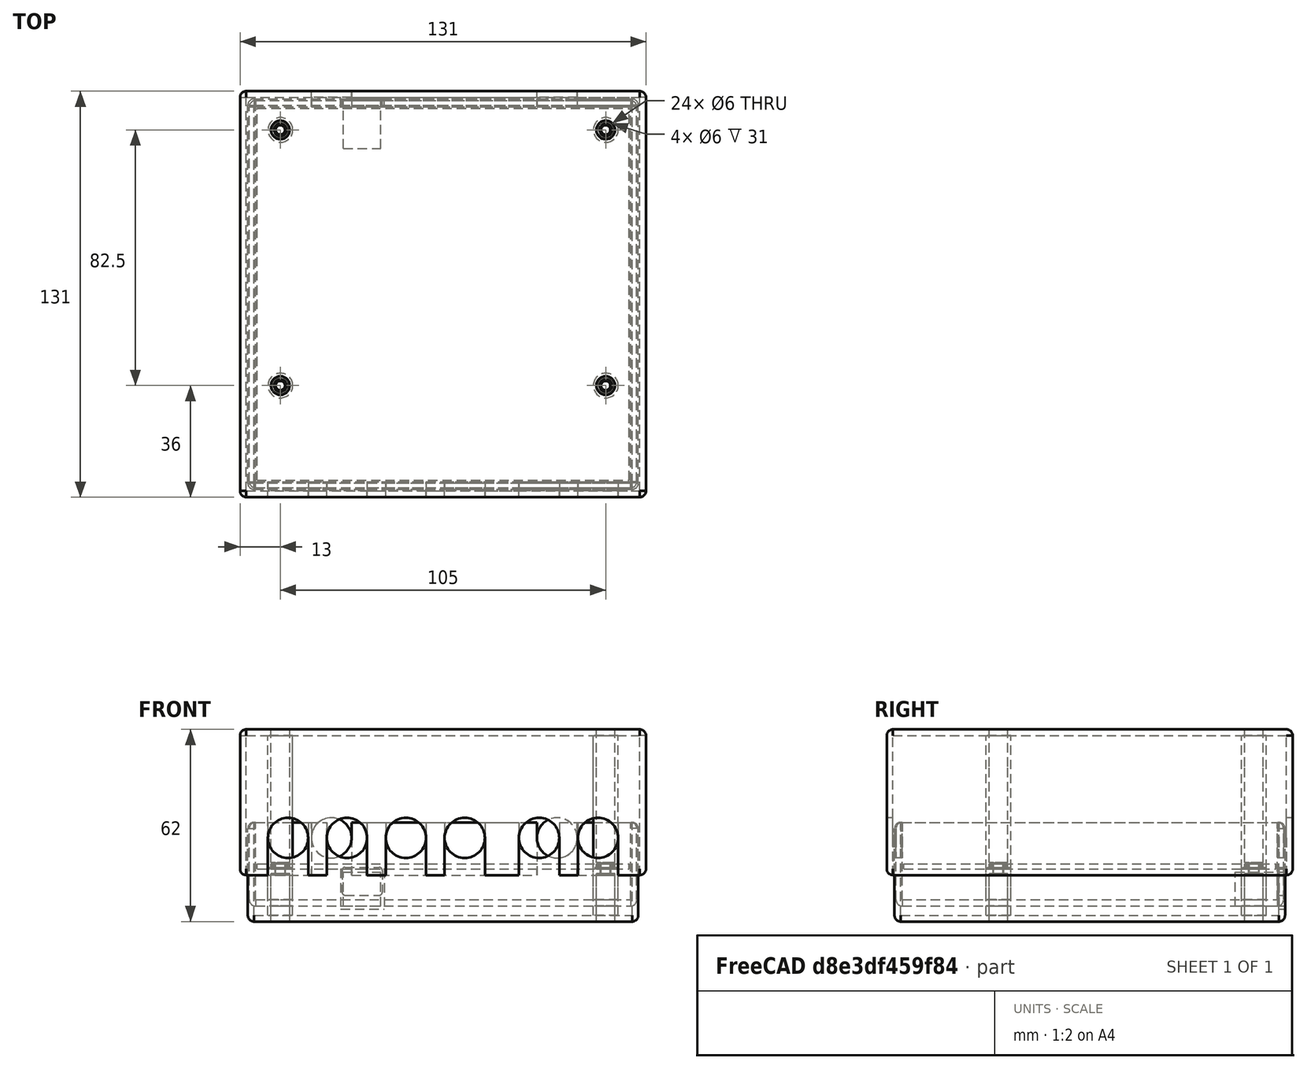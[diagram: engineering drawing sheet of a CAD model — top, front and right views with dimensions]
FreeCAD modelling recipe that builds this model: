
FCSTD DOCUMENT  (FreeCAD 0.14R3700 (Git))
Label: board
License: CC-BY 3.0
LicenseURL: http://creativecommons.org/licenses/by/3.0/
objects: Part::FeaturePython×65, Part::Cylinder×24, Part::MultiFuse×21, Part::Cut×21, Part::Box×17, Part::Offset×4, App::DocumentObjectGroup×3, Part::Feature×1, Part::Fillet×1
note: 154 computed .brp shape members not serialized (recipe doc carries the construction recipe); baked Part::Feature solids carry a one-line shape summary decoded from their .brp

FEATURE [Part::Box] Box  label="Cube"
  Height = 1.6
  Length = 120
  Width = 120
FEATURE [Part::Cylinder] Cylinder
  Angle = 360
  Height = 10
  Placement = pos=(7.5,30.5,-5) rot=(0,0,1;0rad)
  Radius = 3
FEATURE [Part::FeaturePython] Clone  label="Clone of Cylinder"  # Draft clone (typed FeaturePython)
  Objects = -> [Cylinder]
  Placement = pos=(7.5,113,-5) rot=(0,0,1;0rad)
  Scale = (1,1,1)
FEATURE [Part::FeaturePython] Clone001  label="Clone of Cylinder001"  # Draft clone (typed FeaturePython)
  Objects = -> [Cylinder]
  Placement = pos=(112.5,30.5,-5) rot=(0,0,1;0rad)
  Scale = (1,1,1)
FEATURE [Part::FeaturePython] Clone002  label="Clone of Cylinder002"  # Draft clone (typed FeaturePython)
  Objects = -> [Cylinder]
  Placement = pos=(112.5,113,-5) rot=(0,0,1;0rad)
  Scale = (1,1,1)
FEATURE [Part::MultiFuse] Fusion
  Shapes = -> [Cylinder,Clone001,Clone,Clone002]
FEATURE [Part::Cut] Cut  label="board"
  Base = -> Box
  Tool = -> Fusion
FEATURE [Part::Feature] _31_5431_10rfx  label="bnc"
  Placement = pos=(9.975,15.5,2.1) rot=(0.57735,-0.57735,-0.57735;2.0944rad)
  shape: bbox 14.98 x 40.02 x 19.89 mm, 151 faces, 0 solids (baked)
FEATURE [Part::FeaturePython] Clone003  label="bnc02"  # Draft clone (typed FeaturePython)
  Objects = -> [_31_5431_10rfx]
  Placement = pos=(28.975,15.5,2.1) rot=(0.57735,-0.57735,-0.57735;2.0944rad)
  Scale = (1,1,1)
FEATURE [Part::FeaturePython] Clone004  label="bnc03"  # Draft clone (typed FeaturePython)
  Objects = -> [_31_5431_10rfx]
  Placement = pos=(47.975,15.5,2.1) rot=(0.57735,-0.57735,-0.57735;2.0944rad)
  Scale = (1,1,1)
FEATURE [Part::FeaturePython] Clone005  label="bnc04"  # Draft clone (typed FeaturePython)
  Objects = -> [_31_5431_10rfx]
  Placement = pos=(66.975,15.5,2.1) rot=(0.57735,-0.57735,-0.57735;2.0944rad)
  Scale = (1,1,1)
FEATURE [Part::FeaturePython] Clone006  label="bnc05"  # Draft clone (typed FeaturePython)
  Objects = -> [_31_5431_10rfx]
  Placement = pos=(90.975,15.5,2.1) rot=(0.57735,-0.57735,-0.57735;2.0944rad)
  Scale = (1,1,1)
FEATURE [Part::FeaturePython] Clone007  label="bnc06"  # Draft clone (typed FeaturePython)
  Objects = -> [_31_5431_10rfx]
  Placement = pos=(109.975,15.5,2.1) rot=(0.57735,-0.57735,-0.57735;2.0944rad)
  Scale = (1,1,1)
FEATURE [Part::FeaturePython] Clone008  label="bnc07"  # Draft clone (typed FeaturePython)
  Objects = -> [_31_5431_10rfx]
  Placement = pos=(96.775,104.5,2.1) rot=(0.57735,0.57735,0.57735;2.0944rad)
  Scale = (1,1,1)
FEATURE [Part::Box] Box001  label="usb"
  Height = 11
  Length = 12.04
  Placement = pos=(27.851,107,-12) rot=(0,0,1;0rad)
  Width = 16
FEATURE [Part::FeaturePython] Clone009  label="bnc08"  # Draft clone (typed FeaturePython)
  Objects = -> [_31_5431_10rfx]
  Placement = pos=(24.025,104.5,2.1) rot=(0.57735,0.57735,0.57735;2.0944rad)
  Scale = (1,1,1)
FEATURE [Part::Cylinder] Cylinder001
  Angle = 360
  Height = 1.6
  Placement = pos=(7.5,30.5,0) rot=(0,0,1;0rad)
  Radius = 2.5
FEATURE [Part::Cylinder] Cylinder002
  Angle = 360
  Height = 10
  Placement = pos=(7.5,30.5,-9.6) rot=(0,0,1;0rad)
  Radius = 4
FEATURE [Part::MultiFuse] Fusion001
  Shapes = -> [Cylinder001,Cylinder002]
FEATURE [Part::Cylinder] Cylinder003
  Angle = 360
  Height = 9
  Placement = pos=(7.5,30.5,-10.6) rot=(0,0,1;0rad)
  Radius = 3
FEATURE [Part::Cut] Cut001
  Base = -> Fusion001
  Tool = -> Cylinder003
FEATURE [Part::Cylinder] Cylinder004
  Angle = 360
  Height = 9
  Placement = pos=(7.5,30.5,-5.6) rot=(0,0,1;0rad)
  Radius = 1.5
FEATURE [Part::Cut] Cut002
  Base = -> Cut001
  Tool = -> Cylinder004
FEATURE [Part::FeaturePython] Clone010  label="Clone of Cut002"  # Draft clone (typed FeaturePython)
  Objects = -> [Cut002]
  Placement = pos=(105,0,0) rot=(0,0,1;0rad)
  Scale = (1,1,1)
FEATURE [Part::FeaturePython] Clone011  label="Clone of Cut003"  # Draft clone (typed FeaturePython)
  Objects = -> [Cut002]
  Placement = pos=(0,82.5,0) rot=(0,0,1;0rad)
  Scale = (1,1,1)
FEATURE [Part::FeaturePython] Clone012  label="Clone of Cut004"  # Draft clone (typed FeaturePython)
  Objects = -> [Cut002]
  Placement = pos=(105,82.5,0) rot=(0,0,1;0rad)
  Scale = (1,1,1)
FEATURE [Part::Box] Box002  label="Cube001"
  Height = 23
  Length = 121
  Placement = pos=(-0.5,-0.5,-10) rot=(0,0,1;0rad)
  Width = 121
FEATURE [Part::Offset] Offset
  Fill = false
  Intersection = false
  Join = 0
  Mode = 0
  SelfIntersection = false
  Source = -> Box002
  Value = 2
FEATURE [Part::Cylinder] Cylinder005
  Angle = 360
  Height = 10
  Placement = pos=(10,3,10) rot=(1,0,0;1.5708rad)
  Radius = 6.5
FEATURE [Part::Box] Box003  label="Cube002"
  Height = 10
  Length = 13
  Placement = pos=(3.5,-7,10) rot=(0,0,1;0rad)
  Width = 10
FEATURE [Part::MultiFuse] Fusion002  label="bnc-cut"
  Shapes = -> [Cylinder005,Box003]
FEATURE [Part::FeaturePython] Clone013  label="Clone of bnc-cut"  # Draft clone (typed FeaturePython)
  Objects = -> [Fusion002]
  Placement = pos=(19,0,0) rot=(0,0,1;0rad)
  Scale = (1,1,1)
FEATURE [Part::FeaturePython] Clone014  label="Clone of bnc-cut001"  # Draft clone (typed FeaturePython)
  Objects = -> [Fusion002]
  Placement = pos=(38,0,0) rot=(0,0,1;0rad)
  Scale = (1,1,1)
FEATURE [Part::FeaturePython] Clone015  label="Clone of bnc-cut002"  # Draft clone (typed FeaturePython)
  Objects = -> [Fusion002]
  Placement = pos=(57,0,0) rot=(0,0,1;0rad)
  Scale = (1,1,1)
FEATURE [Part::FeaturePython] Clone016  label="Clone of bnc-cut003"  # Draft clone (typed FeaturePython)
  Objects = -> [Fusion002]
  Placement = pos=(81,0,0) rot=(0,0,1;0rad)
  Scale = (1,1,1)
FEATURE [Part::FeaturePython] Clone017  label="Clone of bnc-cut004"  # Draft clone (typed FeaturePython)
  Objects = -> [Fusion002]
  Placement = pos=(100,0,0) rot=(0,0,1;0rad)
  Scale = (1,1,1)
FEATURE [Part::FeaturePython] Clone018  label="Clone of bnc-cut005"  # Draft clone (typed FeaturePython)
  Objects = -> [Fusion002]
  Placement = pos=(14,122,0) rot=(0,0,1;0rad)
  Scale = (1,1,1)
FEATURE [Part::FeaturePython] Clone019  label="Clone of bnc-cut006"  # Draft clone (typed FeaturePython)
  Objects = -> [Fusion002]
  Placement = pos=(86.8,122,0) rot=(0,0,1;0rad)
  Scale = (1,1,1)
FEATURE [Part::Box] Box004  label="Cube003"
  Height = 30
  Length = 121
  Placement = pos=(-0.5,-0.5,-10) rot=(0,0,1;0rad)
  Width = 121
FEATURE [Part::MultiFuse] Fusion003
  Shapes = -> [Clone013,Box004,Clone015,Clone017,Clone018,Clone014,Clone019,Clone016,Fusion002]
FEATURE [Part::Cut] Cut003
  Base = -> Offset
  Tool = -> Fusion003
FEATURE [Part::Box] Box005  label="Cube004"
  Height = 9
  Length = 13
  Placement = pos=(27.4,115,0) rot=(0,0,1;0rad)
  Width = 10
FEATURE [Part::Fillet] Fillet
  Base = -> Box005
  Edges = 12 edges r=1: [Edge1,Edge2,Edge3,Edge4,Edge5,Edge6,Edge7,Edge8,Edge9,Edge10,Edge11,Edge12]
  Placement = pos=(0,0,-8.5) rot=(0,0,1;0rad)
FEATURE [Part::Cut] Cut004
  Base = -> Cut003
  Tool = -> Fillet
FEATURE [Part::Cylinder] Cylinder006
  Angle = 360
  Height = 10
  Placement = pos=(7.5,30.5,-15.6) rot=(0,0,1;0rad)
  Radius = 4
FEATURE [Part::FeaturePython] Clone020  label="Clone of Cylinder006"  # Draft clone (typed FeaturePython)
  Objects = -> [Cylinder006]
  Placement = pos=(7.5,113,-15.6) rot=(0,0,1;0rad)
  Scale = (1,1,1)
FEATURE [Part::FeaturePython] Clone021  label="Clone of Cylinder007"  # Draft clone (typed FeaturePython)
  Objects = -> [Cylinder006]
  Placement = pos=(112.5,30.5,-15.6) rot=(0,0,1;0rad)
  Scale = (1,1,1)
FEATURE [Part::FeaturePython] Clone022  label="Clone of Cylinder008"  # Draft clone (typed FeaturePython)
  Objects = -> [Cylinder006]
  Placement = pos=(112.5,113,-15.6) rot=(0,0,1;0rad)
  Scale = (1,1,1)
FEATURE [Part::MultiFuse] Fusion004
  Shapes = -> [Cylinder006,Clone020,Clone021,Clone022]
FEATURE [Part::Cut] Cut005
  Base = -> Cut004
  Tool = -> Fusion004
FEATURE [Part::MultiFuse] Fusion005
  Shapes = -> [Cut002,Clone010,Clone011,Clone012,Cut005]
FEATURE [Part::Box] Box006  label="Cube005"
  Height = 40
  Length = 126
  Placement = pos=(-3,-3,3) rot=(0,0,1;0rad)
  Width = 126
FEATURE [Part::Box] Box007  label="Cube006"
  Height = 40
  Length = 34
  Placement = pos=(35,115,2) rot=(0,0,1;0rad)
  Width = 2
FEATURE [App::DocumentObjectGroup] Group  label="pcb"
  Group = -> [Cut,_31_5431_10rfx,Clone003,Clone004,Clone005,Clone006,Clone007,Clone008,Box001,Clone009,Box007]
FEATURE [Part::Offset] Offset001
  Fill = false
  Intersection = false
  Join = 0
  Mode = 0
  SelfIntersection = false
  Source = -> Box006
  Value = 2
FEATURE [Part::Box] Box008  label="Cube007"
  Height = 45
  Length = 126
  Placement = pos=(-3,-3,-2) rot=(0,0,1;0rad)
  Width = 126
FEATURE [Part::Cut] Cut006
  Base = -> Offset001
  Tool = -> Box008
FEATURE [Part::Cylinder] Cylinder007
  Angle = 360
  Height = 42
  Placement = pos=(7.5,30.5,1.6) rot=(0,0,1;0rad)
  Radius = 4
FEATURE [Part::Cylinder] Cylinder008
  Angle = 360
  Height = 9
  Placement = pos=(7.5,30.5,-0.6) rot=(0,0,1;0rad)
  Radius = 1.5
FEATURE [Part::Cylinder] Cylinder009
  Angle = 360
  Height = 43
  Placement = pos=(7.5,30.5,3.4) rot=(0,0,1;0rad)
  Radius = 3
FEATURE [Part::Cut] Cut007
  Base = -> Cylinder007
  Tool = -> Cylinder008
FEATURE [Part::FeaturePython] Clone023  label="Clone of Cut007"  # Draft clone (typed FeaturePython)
  Objects = -> [Cut007]
  Placement = pos=(105,0,0) rot=(0,0,1;0rad)
  Scale = (1,1,1)
FEATURE [Part::FeaturePython] Clone024  label="Clone of Cut008"  # Draft clone (typed FeaturePython)
  Objects = -> [Cut007]
  Placement = pos=(105,82.5,0) rot=(0,0,1;0rad)
  Scale = (1,1,1)
FEATURE [Part::FeaturePython] Clone025  label="Clone of Cut009"  # Draft clone (typed FeaturePython)
  Objects = -> [Cut007]
  Placement = pos=(0,82.5,0) rot=(0,0,1;0rad)
  Scale = (1,1,1)
FEATURE [Part::MultiFuse] Fusion006
  Shapes = -> [Cut006,Clone023,Cut007,Clone024,Clone025]
FEATURE [Part::FeaturePython] Clone026  label="Clone of Cylinder009"  # Draft clone (typed FeaturePython)
  Objects = -> [Cylinder009]
  Placement = pos=(112.5,30.5,3.4) rot=(0,0,1;0rad)
  Scale = (1,1,1)
FEATURE [Part::FeaturePython] Clone027  label="Clone of Cylinder010"  # Draft clone (typed FeaturePython)
  Objects = -> [Cylinder009]
  Placement = pos=(112.5,113,3.4) rot=(0,0,1;0rad)
  Scale = (1,1,1)
FEATURE [Part::FeaturePython] Clone028  label="Clone of Cylinder011"  # Draft clone (typed FeaturePython)
  Objects = -> [Cylinder009]
  Placement = pos=(7.5,113,3.4) rot=(0,0,1;0rad)
  Scale = (1,1,1)
FEATURE [Part::MultiFuse] Fusion007
  Shapes = -> [Cylinder009,Clone026,Clone027,Clone028]
FEATURE [Part::Cut] Cut008
  Base = -> Fusion006
  Tool = -> Fusion007
FEATURE [Part::Cylinder] Cylinder010
  Angle = 360
  Height = 3
  Placement = pos=(7.5,30.5,-12) rot=(0,0,1;0rad)
  Radius = 4
FEATURE [Part::Cylinder] Cylinder011
  Angle = 360
  Height = 8.6
  Placement = pos=(7.5,30.5,-15) rot=(0,0,1;0rad)
  Radius = 3
FEATURE [Part::Cut] Cut009
  Base = -> Cylinder010
  Tool = -> Cylinder011
FEATURE [Part::FeaturePython] Clone029  label="Clone of Cut010"  # Draft clone (typed FeaturePython)
  Objects = -> [Cut009]
  Placement = pos=(0,82.5,0) rot=(0,0,1;0rad)
  Scale = (1,1,1)
FEATURE [Part::FeaturePython] Clone030  label="Clone of Cut011"  # Draft clone (typed FeaturePython)
  Objects = -> [Cut009]
  Placement = pos=(105,0,0) rot=(0,0,1;0rad)
  Scale = (1,1,1)
FEATURE [Part::FeaturePython] Clone031  label="Clone of Cut012"  # Draft clone (typed FeaturePython)
  Objects = -> [Cut009]
  Placement = pos=(105,82.5,0) rot=(0,0,1;0rad)
  Scale = (1,1,1)
FEATURE [Part::MultiFuse] Fusion008
  Shapes = -> [Cut009,Clone029,Clone031,Clone030,Fusion005]
FEATURE [App::DocumentObjectGroup] Group001  label="bottom"
  Group = -> [Fusion005,Cut009,Clone029,Clone031,Clone030,Fusion008]
FEATURE [Part::Cylinder] Cylinder012
  Angle = 360
  Height = 10
  Placement = pos=(10,3,10) rot=(1,0,0;1.5708rad)
  Radius = 6.5
FEATURE [Part::Box] Box009  label="Cube008"
  Height = 10
  Length = 13
  Placement = pos=(3.5,-7,0) rot=(0,0,1;0rad)
  Width = 10
FEATURE [Part::MultiFuse] Fusion009  label="bnc-cut-top"
  Shapes = -> [Cylinder012,Box009]
FEATURE [Part::FeaturePython] Clone032  label="Clone of bnc-cut-top"  # Draft clone (typed FeaturePython)
  Objects = -> [Fusion009]
  Placement = pos=(19,0,0) rot=(0,0,1;0rad)
  Scale = (1,1,1)
FEATURE [Part::FeaturePython] Clone033  label="Clone of bnc-cut-top001"  # Draft clone (typed FeaturePython)
  Objects = -> [Fusion009]
  Placement = pos=(38,0,0) rot=(0,0,1;0rad)
  Scale = (1,1,1)
FEATURE [Part::FeaturePython] Clone034  label="Clone of bnc-cut-top002"  # Draft clone (typed FeaturePython)
  Objects = -> [Fusion009]
  Placement = pos=(57,0,0) rot=(0,0,1;0rad)
  Scale = (1,1,1)
FEATURE [Part::FeaturePython] Clone035  label="Clone of bnc-cut-top003"  # Draft clone (typed FeaturePython)
  Objects = -> [Fusion009]
  Placement = pos=(81,0,0) rot=(0,0,1;0rad)
  Scale = (1,1,1)
FEATURE [Part::FeaturePython] Clone036  label="Clone of bnc-cut-top004"  # Draft clone (typed FeaturePython)
  Objects = -> [Fusion009]
  Placement = pos=(100,0,0) rot=(0,0,1;0rad)
  Scale = (1,1,1)
FEATURE [Part::FeaturePython] Clone037  label="Clone of bnc-cut-top005"  # Draft clone (typed FeaturePython)
  Objects = -> [Fusion009]
  Placement = pos=(14,125,0) rot=(0,0,1;0rad)
  Scale = (1,1,1)
FEATURE [Part::FeaturePython] Clone038  label="Clone of bnc-cut-top006"  # Draft clone (typed FeaturePython)
  Objects = -> [Fusion009]
  Placement = pos=(86.8,125,0) rot=(0,0,1;0rad)
  Scale = (1,1,1)
FEATURE [Part::MultiFuse] Fusion010
  Shapes = -> [Fusion009,Clone033,Clone032,Clone034,Clone035,Clone036,Clone037,Clone038]
FEATURE [Part::Cut] Cut010
  Base = -> Cut008
  Tool = -> Fusion010
FEATURE [App::DocumentObjectGroup] Group002  label="top"
  Group = -> [Cut010]
FEATURE [Part::Box] Box010  label="Cube009"
  Height = 28
  Length = 122
  Placement = pos=(-1,-1,-15) rot=(0,0,1;0rad)
  Width = 122
FEATURE [Part::Offset] Offset002
  Fill = false
  Intersection = false
  Join = 0
  Mode = 0
  SelfIntersection = false
  Source = -> Box010
  Value = 2
FEATURE [Part::Box] Box011  label="Cube010"
  Height = 37
  Length = 122
  Placement = pos=(-1,-1,-15) rot=(0,0,1;0rad)
  Width = 122
FEATURE [Part::Cut] Cut011
  Base = -> Offset002
  Tool = -> Box011
FEATURE [Part::Box] Box012  label="Cube011"
  Height = 13
  Length = 14
  Placement = pos=(27,116,-13) rot=(0,0,1;0rad)
  Width = 10
FEATURE [Part::Cut] Cut012
  Base = -> Cut011
  Tool = -> Box012
FEATURE [Part::Cylinder] Cylinder013
  Angle = 360
  Height = 10
  Placement = pos=(10,2,10) rot=(1,0,0;1.5708rad)
  Radius = 6.5
FEATURE [Part::Box] Box013  label="Cube012"
  Height = 10
  Length = 13
  Placement = pos=(3.5,-8,10) rot=(0,0,1;0rad)
  Width = 10
FEATURE [Part::MultiFuse] Fusion011  label="bnc-cut001"
  Shapes = -> [Cylinder013,Box013]
FEATURE [Part::FeaturePython] Clone039  label="Clone of bnc-cut007"  # Draft clone (typed FeaturePython)
  Objects = -> [Fusion011]
  Placement = pos=(19,0,0) rot=(0,0,1;0rad)
  Scale = (1,1,1)
FEATURE [Part::FeaturePython] Clone040  label="Clone of bnc-cut008"  # Draft clone (typed FeaturePython)
  Objects = -> [Fusion011]
  Placement = pos=(38,0,0) rot=(0,0,1;0rad)
  Scale = (1,1,1)
FEATURE [Part::FeaturePython] Clone041  label="Clone of bnc-cut009"  # Draft clone (typed FeaturePython)
  Objects = -> [Fusion011]
  Placement = pos=(57,0,0) rot=(0,0,1;0rad)
  Scale = (1,1,1)
FEATURE [Part::FeaturePython] Clone042  label="Clone of bnc-cut010"  # Draft clone (typed FeaturePython)
  Objects = -> [Fusion011]
  Placement = pos=(81,0,0) rot=(0,0,1;0rad)
  Scale = (1,1,1)
FEATURE [Part::FeaturePython] Clone043  label="Clone of bnc-cut011"  # Draft clone (typed FeaturePython)
  Objects = -> [Fusion011]
  Placement = pos=(100,0,0) rot=(0,0,1;0rad)
  Scale = (1,1,1)
FEATURE [Part::FeaturePython] Clone044  label="Clone of bnc-cut012"  # Draft clone (typed FeaturePython)
  Objects = -> [Fusion011]
  Placement = pos=(14,124,0) rot=(0,0,1;0rad)
  Scale = (1,1,1)
FEATURE [Part::FeaturePython] Clone045  label="Clone of bnc-cut013"  # Draft clone (typed FeaturePython)
  Objects = -> [Fusion011]
  Placement = pos=(86.8,124,0) rot=(0,0,1;0rad)
  Scale = (1,1,1)
FEATURE [Part::MultiFuse] Fusion012  label="bnc-full-cut"
  Shapes = -> [Fusion011,Clone042,Clone043,Clone044,Clone041,Clone045,Clone040,Clone039]
FEATURE [Part::Cut] Cut013
  Base = -> Cut012
  Tool = -> Fusion012
FEATURE [Part::Cylinder] Cylinder014
  Angle = 360
  Height = 10
  Placement = pos=(7.5,30.5,-4) rot=(0,0,1;0rad)
  Radius = 1.7
FEATURE [Part::Cylinder] Cylinder015
  Angle = 360
  Height = 11.6
  Placement = pos=(7.5,30.5,-10) rot=(0,0,1;0rad)
  Radius = 2.5
FEATURE [Part::Cylinder] Cylinder016
  Angle = 360
  Height = 15
  Placement = pos=(7.5,30.5,-15) rot=(0,0,1;0rad)
  Radius = 4
FEATURE [Part::MultiFuse] Fusion013
  Shapes = -> [Cylinder015,Cylinder016]
FEATURE [Part::Cylinder] Cylinder017
  Angle = 360
  Height = 15
  Placement = pos=(7.5,30.5,-17) rot=(0,0,1;0rad)
  Radius = 3
FEATURE [Part::MultiFuse] Fusion014
  Shapes = -> [Cylinder017,Cylinder014]
FEATURE [Part::Cut] Cut014  label="stand-bottom"
  Base = -> Fusion013
  Tool = -> Fusion014
FEATURE [Part::FeaturePython] Clone046  label="Clone of stand-bottom"  # Draft clone (typed FeaturePython)
  Objects = -> [Cut014]
  Placement = pos=(105,0,0) rot=(0,0,1;0rad)
  Scale = (1,1,1)
FEATURE [Part::FeaturePython] Clone047  label="Clone of stand-bottom001"  # Draft clone (typed FeaturePython)
  Objects = -> [Cut014]
  Placement = pos=(105,82.5,0) rot=(0,0,1;0rad)
  Scale = (1,1,1)
FEATURE [Part::FeaturePython] Clone048  label="Clone of stand-bottom002"  # Draft clone (typed FeaturePython)
  Objects = -> [Cut014]
  Placement = pos=(0,82.5,0) rot=(0,0,1;0rad)
  Scale = (1,1,1)
FEATURE [Part::MultiFuse] Fusion015
  Shapes = -> [Cut013,Cut014,Clone046,Clone047,Clone048]
FEATURE [Part::Cylinder] Cylinder018
  Angle = 360
  Height = 15
  Placement = pos=(7.5,30.5,-20) rot=(0,0,1;0rad)
  Radius = 3
FEATURE [Part::FeaturePython] Clone049  label="Clone of Cylinder018"  # Draft clone (typed FeaturePython)
  Objects = -> [Cylinder018]
  Placement = pos=(112.5,30.5,-20) rot=(0,0,1;0rad)
  Scale = (1,1,1)
FEATURE [Part::FeaturePython] Clone050  label="Clone of Cylinder019"  # Draft clone (typed FeaturePython)
  Objects = -> [Cylinder018]
  Placement = pos=(112.5,113,-20) rot=(0,0,1;0rad)
  Scale = (1,1,1)
FEATURE [Part::FeaturePython] Clone051  label="Clone of Cylinder020"  # Draft clone (typed FeaturePython)
  Objects = -> [Cylinder018]
  Placement = pos=(7.5,113,-20) rot=(0,0,1;0rad)
  Scale = (1,1,1)
FEATURE [Part::MultiFuse] Fusion016
  Shapes = -> [Cylinder018,Clone049,Clone050,Clone051]
FEATURE [Part::Cut] Cut015  label="bottom-v02"
  Base = -> Fusion015
  Tool = -> Fusion016
FEATURE [Part::Box] Box014  label="Cube013"
  Height = 43
  Length = 127
  Placement = pos=(-3.5,-3.5,0) rot=(0,0,1;0rad)
  Width = 127
FEATURE [Part::Offset] Offset003
  Fill = false
  Intersection = false
  Join = 0
  Mode = 0
  SelfIntersection = false
  Source = -> Box014
  Value = 2
FEATURE [Part::Box] Box015  label="Cube014"
  Height = 46
  Length = 127
  Placement = pos=(-3.5,-3.5,-3) rot=(0,0,1;0rad)
  Width = 127
FEATURE [Part::Cut] Cut016
  Base = -> Offset003
  Tool = -> Box015
FEATURE [Part::Cylinder] Cylinder019
  Angle = 360
  Height = 10
  Placement = pos=(10,0,10) rot=(1,0,0;1.5708rad)
  Radius = 6.5
FEATURE [Part::Box] Box016  label="Cube015"
  Height = 14
  Length = 13
  Placement = pos=(3.5,-10,-4) rot=(0,0,1;0rad)
  Width = 10
FEATURE [Part::MultiFuse] Fusion017  label="bnc-cut-top001"
  Shapes = -> [Cylinder019,Box016]
FEATURE [Part::FeaturePython] Clone052  label="Clone of bnc-cut-top007"  # Draft clone (typed FeaturePython)
  Objects = -> [Fusion017]
  Placement = pos=(19,0,0) rot=(0,0,1;0rad)
  Scale = (1,1,1)
FEATURE [Part::FeaturePython] Clone053  label="Clone of bnc-cut-top008"  # Draft clone (typed FeaturePython)
  Objects = -> [Fusion017]
  Placement = pos=(38,0,0) rot=(0,0,1;0rad)
  Scale = (1,1,1)
FEATURE [Part::FeaturePython] Clone054  label="Clone of bnc-cut-top009"  # Draft clone (typed FeaturePython)
  Objects = -> [Fusion017]
  Placement = pos=(57,0,0) rot=(0,0,1;0rad)
  Scale = (1,1,1)
FEATURE [Part::FeaturePython] Clone055  label="Clone of bnc-cut-top010"  # Draft clone (typed FeaturePython)
  Objects = -> [Fusion017]
  Placement = pos=(81,0,0) rot=(0,0,1;0rad)
  Scale = (1,1,1)
FEATURE [Part::FeaturePython] Clone056  label="Clone of bnc-cut-top011"  # Draft clone (typed FeaturePython)
  Objects = -> [Fusion017]
  Placement = pos=(100,0,0) rot=(0,0,1;0rad)
  Scale = (1,1,1)
FEATURE [Part::FeaturePython] Clone057  label="Clone of bnc-cut-top012"  # Draft clone (typed FeaturePython)
  Objects = -> [Fusion017]
  Placement = pos=(14,129,0) rot=(0,0,1;0rad)
  Scale = (1,1,1)
FEATURE [Part::FeaturePython] Clone058  label="Clone of bnc-cut-top013"  # Draft clone (typed FeaturePython)
  Objects = -> [Fusion017]
  Placement = pos=(86.8,129,0) rot=(0,0,1;0rad)
  Scale = (1,1,1)
FEATURE [Part::MultiFuse] Fusion018
  Shapes = -> [Fusion017,Clone052,Clone053,Clone054,Clone055,Clone056,Clone057,Clone058]
FEATURE [Part::Cut] Cut017
  Base = -> Cut016
  Tool = -> Fusion018
FEATURE [Part::Cylinder] Cylinder020
  Angle = 360
  Height = 44
  Placement = pos=(7.5,30.5,2) rot=(0,0,1;0rad)
  Radius = 3
FEATURE [Part::Cylinder] Cylinder021
  Angle = 360
  Height = 44
  Placement = pos=(7.5,30.5,0) rot=(0,0,1;0rad)
  Radius = 4
FEATURE [Part::Cut] Cut018
  Base = -> Cylinder021
  Tool = -> Cylinder020
FEATURE [Part::Cylinder] Cylinder022
  Angle = 360
  Height = 44
  Placement = pos=(7.5,30.5,-5) rot=(0,0,1;0rad)
  Radius = 2
FEATURE [Part::Cut] Cut019  label="stand-top"
  Base = -> Cut018
  Tool = -> Cylinder022
FEATURE [Part::FeaturePython] Clone059  label="Clone of stand-top"  # Draft clone (typed FeaturePython)
  Objects = -> [Cut019]
  Placement = pos=(105,0,0) rot=(0,0,1;0rad)
  Scale = (1,1,1)
FEATURE [Part::FeaturePython] Clone060  label="Clone of stand-top001"  # Draft clone (typed FeaturePython)
  Objects = -> [Cut019]
  Placement = pos=(105,82.5,0) rot=(0,0,1;0rad)
  Scale = (1,1,1)
FEATURE [Part::FeaturePython] Clone061  label="Clone of stand-top002"  # Draft clone (typed FeaturePython)
  Objects = -> [Cut019]
  Placement = pos=(0,82.5,0) rot=(0,0,1;0rad)
  Scale = (1,1,1)
FEATURE [Part::MultiFuse] Fusion019
  Shapes = -> [Cut017,Cut019,Clone059,Clone060,Clone061]
FEATURE [Part::Cylinder] Cylinder023
  Angle = 360
  Height = 19
  Placement = pos=(7.5,30.5,33) rot=(0,0,1;0rad)
  Radius = 3
FEATURE [Part::FeaturePython] Clone062  label="Clone of Cylinder023"  # Draft clone (typed FeaturePython)
  Objects = -> [Cylinder023]
  Placement = pos=(7.5,113,33) rot=(0,0,1;0rad)
  Scale = (1,1,1)
FEATURE [Part::FeaturePython] Clone063  label="Clone of Cylinder024"  # Draft clone (typed FeaturePython)
  Objects = -> [Cylinder023]
  Placement = pos=(112.5,113,33) rot=(0,0,1;0rad)
  Scale = (1,1,1)
FEATURE [Part::FeaturePython] Clone064  label="Clone of Cylinder025"  # Draft clone (typed FeaturePython)
  Objects = -> [Cylinder023]
  Placement = pos=(112.5,30.5,33) rot=(0,0,1;0rad)
  Scale = (1,1,1)
FEATURE [Part::MultiFuse] Fusion020
  Shapes = -> [Cylinder023,Clone063,Clone062,Clone064]
FEATURE [Part::Cut] Cut020  label="top-v2"
  Base = -> Fusion019
  Tool = -> Fusion020
